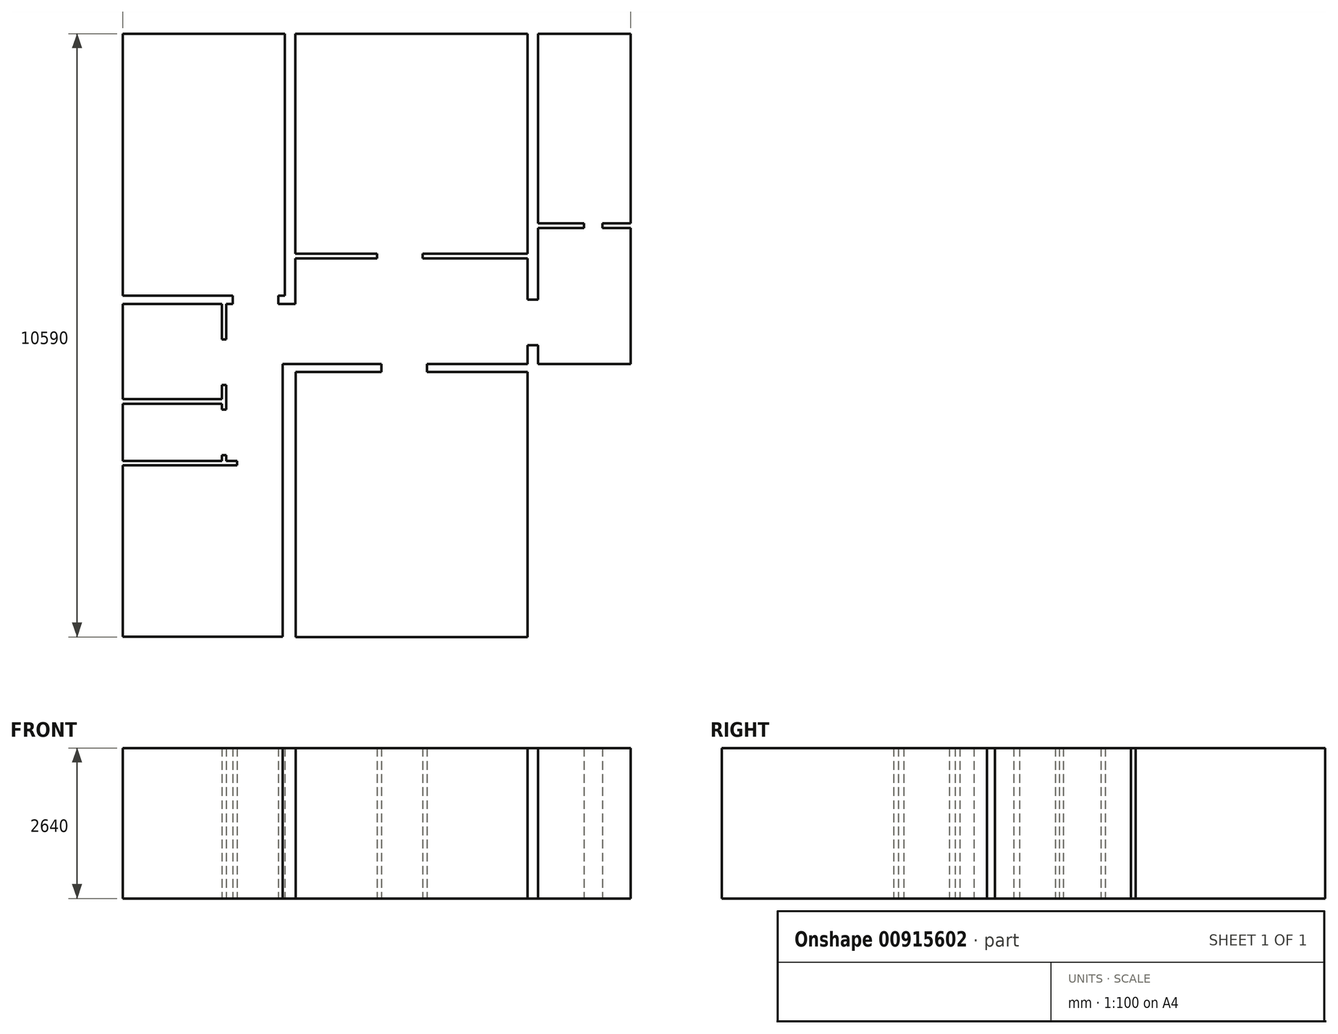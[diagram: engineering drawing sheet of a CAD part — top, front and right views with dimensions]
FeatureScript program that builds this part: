
annotation { "Feature Type Name" : "Feature", "Feature Type Description" : "" }
export const myFeature = defineFeature(function(context is Context, id is Id, definition is map)
    precondition{}
    {
        {
            var Q0;
            Q0=qCreatedBy(makeId("Top.planeOp"),FACE);
            var sketch = newSketch(context, id + "F0", { "sketchPlane" : qUnion([Q0])});
            skLineSegment(sketch, "E0", {"start": v(0, 0) * mm, "end": v(2810, 0) * mm});
            skLineSegment(sketch, "E1", {"start": v(3040, -3.85) * mm, "end": v(3040, 4646.15) * mm});
            skLineSegment(sketch, "E2", {"start": v(3040, 4646.15) * mm, "end": v(4540, 4646.15) * mm});
            skLineSegment(sketch, "E3", {"start": v(4540, 4646.15) * mm, "end": v(4540, 4786.15) * mm});
            skLineSegment(sketch, "E4", {"start": v(4540, 4786.15) * mm, "end": v(2810, 4786.15) * mm});
            skLineSegment(sketch, "E5", {"start": v(3040, -3.85) * mm, "end": v(7110, -3.85) * mm});
            skLineSegment(sketch, "E6", {"start": v(7110, -3.85) * mm, "end": v(7110, 4646.15) * mm});
            skLineSegment(sketch, "E7", {"start": v(7110, 4646.15) * mm, "end": v(5340, 4646.15) * mm});
            skLineSegment(sketch, "E8", {"start": v(5340, 4646.15) * mm, "end": v(5340, 4786.15) * mm});
            skLineSegment(sketch, "E9", {"start": v(5340, 4786.15) * mm, "end": v(7110, 4786.15) * mm});
            skLineSegment(sketch, "E10", {"start": v(7110, 4786.15) * mm, "end": v(7110, 5120) * mm});
            skLineSegment(sketch, "E11", {"start": v(7110, 5120) * mm, "end": v(7290, 5120) * mm});
            skLineSegment(sketch, "E12", {"start": v(7290, 5120) * mm, "end": v(7290, 4786.15) * mm});
            skLineSegment(sketch, "E13", {"start": v(7290, 4786.15) * mm, "end": v(8920, 4786.15) * mm});
            skLineSegment(sketch, "E14", {"start": v(8920, 4786.15) * mm, "end": v(8920, 7176.15) * mm});
            skLineSegment(sketch, "E15", {"start": v(8920, 7176.15) * mm, "end": v(8421.7, 7176.15) * mm});
            skLineSegment(sketch, "E16", {"start": v(8421.7, 7176.15) * mm, "end": v(8421.7, 7256.15) * mm});
            skLineSegment(sketch, "E17", {"start": v(8421.7, 7256.15) * mm, "end": v(8920, 7256.15) * mm});
            skLineSegment(sketch, "E18", {"start": v(8920, 7256.15) * mm, "end": v(8920, 10586.15) * mm});
            skLineSegment(sketch, "E19", {"start": v(8920, 10586.15) * mm, "end": v(7290, 10586.15) * mm});
            skLineSegment(sketch, "E20", {"start": v(7290, 10586.15) * mm, "end": v(7290, 7256.15) * mm});
            skLineSegment(sketch, "E21", {"start": v(7290, 7256.15) * mm, "end": v(8097.23, 7256.15) * mm});
            skLineSegment(sketch, "E22", {"start": v(8097.23, 7256.15) * mm, "end": v(8097.23, 7176.15) * mm});
            skLineSegment(sketch, "E23", {"start": v(8097.23, 7176.15) * mm, "end": v(7290, 7176.15) * mm});
            skLineSegment(sketch, "E24", {"start": v(7290, 7176.15) * mm, "end": v(7290, 5920) * mm});
            skLineSegment(sketch, "E25", {"start": v(7290, 5920) * mm, "end": v(7110, 5920) * mm});
            skLineSegment(sketch, "E26", {"start": v(7110, 5920) * mm, "end": v(7110, 6646.15) * mm});
            skLineSegment(sketch, "E27", {"start": v(7110, 6646.15) * mm, "end": v(5264.75, 6646.15) * mm});
            skLineSegment(sketch, "E28", {"start": v(5264.75, 6646.15) * mm, "end": v(5264.75, 6726.15) * mm});
            skLineSegment(sketch, "E29", {"start": v(5264.75, 6726.15) * mm, "end": v(7110, 6726.15) * mm});
            skLineSegment(sketch, "E30", {"start": v(7110, 6726.15) * mm, "end": v(7110, 10586.15) * mm});
            skLineSegment(sketch, "E31", {"start": v(7110, 10586.15) * mm, "end": v(3030, 10586.15) * mm});
            skLineSegment(sketch, "E32", {"start": v(3030, 10586.15) * mm, "end": v(3030, 6726.15) * mm});
            skLineSegment(sketch, "E33", {"start": v(3030, 6726.15) * mm, "end": v(4464.75, 6726.15) * mm});
            skLineSegment(sketch, "E34", {"start": v(4464.75, 6726.15) * mm, "end": v(4464.75, 6646.15) * mm});
            skLineSegment(sketch, "E35", {"start": v(4464.75, 6646.15) * mm, "end": v(3030, 6646.15) * mm});
            skLineSegment(sketch, "E36", {"start": v(3030, 6646.15) * mm, "end": v(3030, 5846.15) * mm});
            skLineSegment(sketch, "E37", {"start": v(3030, 5846.15) * mm, "end": v(2730, 5846.15) * mm});
            skLineSegment(sketch, "E38", {"start": v(2730, 5846.15) * mm, "end": v(2730, 5986.15) * mm});
            skLineSegment(sketch, "E39", {"start": v(2730, 5986.15) * mm, "end": v(2850, 5986.15) * mm});
            skLineSegment(sketch, "E40", {"start": v(2850, 5986.15) * mm, "end": v(2850, 10586.15) * mm});
            skLineSegment(sketch, "E41", {"start": v(2850, 10586.15) * mm, "end": v(0, 10586.15) * mm});
            skLineSegment(sketch, "E42", {"start": v(0, 10586.15) * mm, "end": v(0, 5986.15) * mm});
            skLineSegment(sketch, "E43", {"start": v(0, 5986.15) * mm, "end": v(1930, 5986.15) * mm});
            skLineSegment(sketch, "E44", {"start": v(1930, 5986.15) * mm, "end": v(1930, 5846.15) * mm});
            skLineSegment(sketch, "E45", {"start": v(0, 0) * mm, "end": v(0, 3010) * mm});
            skLineSegment(sketch, "E46", {"start": v(0, 3010) * mm, "end": v(2010, 3010) * mm});
            skLineSegment(sketch, "E47", {"start": v(2010, 3010) * mm, "end": v(2010, 3090) * mm});
            skLineSegment(sketch, "E48", {"start": v(2010, 3090) * mm, "end": v(1820, 3090) * mm});
            skLineSegment(sketch, "E49", {"start": v(1820, 3090) * mm, "end": v(1820, 3190) * mm});
            skLineSegment(sketch, "E50", {"start": v(2810, 4786.15) * mm, "end": v(2810, 0) * mm});
            skLineSegment(sketch, "E51", {"start": v(1820, 3190) * mm, "end": v(1740, 3190) * mm});
            skLineSegment(sketch, "E52", {"start": v(1740, 3190) * mm, "end": v(1740, 3090) * mm});
            skLineSegment(sketch, "E53", {"start": v(1740, 3090) * mm, "end": v(0, 3090) * mm});
            skLineSegment(sketch, "E54", {"start": v(1740, 3990) * mm, "end": v(1820, 3990) * mm});
            skLineSegment(sketch, "E55", {"start": v(1820, 3990) * mm, "end": v(1820, 4420) * mm});
            skLineSegment(sketch, "E56", {"start": v(1820, 4420) * mm, "end": v(1740, 4420) * mm});
            skLineSegment(sketch, "E57", {"start": v(1740, 4420) * mm, "end": v(1740, 4170) * mm});
            skLineSegment(sketch, "E58", {"start": v(1740, 4170) * mm, "end": v(0, 4170) * mm});
            skLineSegment(sketch, "E59", {"start": v(1740, 3990) * mm, "end": v(1740, 4090) * mm});
            skLineSegment(sketch, "E60", {"start": v(1740, 4090) * mm, "end": v(0, 4090) * mm});
            skLineSegment(sketch, "E61", {"start": v(0, 4090) * mm, "end": v(0, 3090) * mm});
            skLineSegment(sketch, "E62", {"start": v(1930, 5846.15) * mm, "end": v(1820, 5846.15) * mm});
            skLineSegment(sketch, "E63", {"start": v(1820, 5846.15) * mm, "end": v(1820, 5220) * mm});
            skLineSegment(sketch, "E64", {"start": v(1820, 5220) * mm, "end": v(1740, 5220) * mm});
            skLineSegment(sketch, "E65", {"start": v(1740, 5220) * mm, "end": v(1740, 5846.15) * mm});
            skLineSegment(sketch, "E66", {"start": v(1740, 5846.15) * mm, "end": v(0, 5846.15) * mm});
            skLineSegment(sketch, "E67", {"start": v(0, 5846.15) * mm, "end": v(0, 4170) * mm});
            skSolve(sketch);
        }
        {
            var Q0;
            Q0 = qSketchRegion(id + "F0", true);
            extrude(context, id + "F1", {"entities" : qUnion([Q0]), "depth" : 2640 * mm, "offsetDistance" : 25 * mm});
        }
    });
